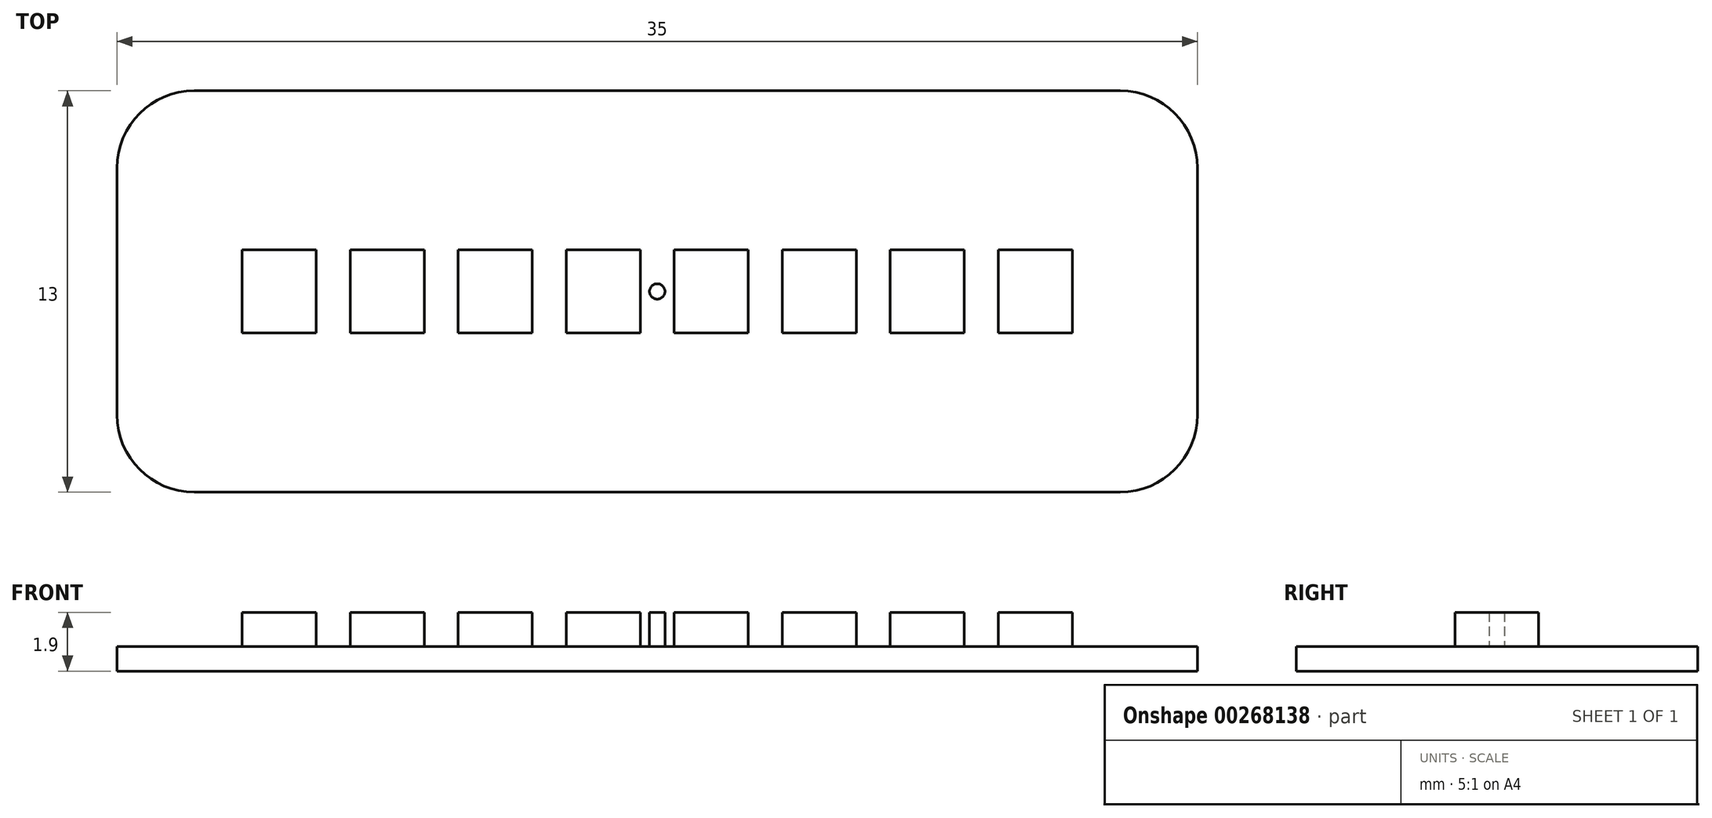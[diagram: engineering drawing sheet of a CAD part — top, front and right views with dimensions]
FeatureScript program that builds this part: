
annotation { "Feature Type Name" : "Feature", "Feature Type Description" : "" }
export const myFeature = defineFeature(function(context is Context, id is Id, definition is map)
    precondition{}
    {
        {
            var Q0;
            Q0=qCreatedBy(makeId("Top.planeOp"),FACE);
            var sketch = newSketch(context, id + "F0", { "sketchPlane" : qUnion([Q0])});
            skLineSegment(sketch, "E0.bottom", {"start": v(-17.5, 6.5) * mm, "end": v(17.5, 6.5) * mm});
            skLineSegment(sketch, "E0.top", {"start": v(-17.5, -6.5) * mm, "end": v(17.5, -6.5) * mm});
            skLineSegment(sketch, "E0.left", {"start": v(-17.5, 6.5) * mm, "end": v(-17.5, -6.5) * mm});
            skLineSegment(sketch, "E0.right", {"start": v(17.5, 6.5) * mm, "end": v(17.5, -6.5) * mm});
            skPoint(sketch, "E0.middle", {"position": v(0, 0) * mm});
            skPoint(sketch, "E1.endSnap0", {"position": v(-17.5, 0) * mm});
            skLineSegment(sketch, "E2", {"start": v(0, 0) * mm, "end": v(0, 0) * mm});
            skSolve(sketch);
        }
        {
            var Q0;
            Q0=makeQuery(id+"F0.imprint","IMPRINT",FACE,{"disambiguationData":[TD([[makeQuery(id+"F0.imprint","IMPRINT",EDGE,{"derivedFrom":sQuery(id+"F0.wireOp",EDGE,"E0.bottom")}),-1.0]])]});
            extrude(context, id + "F1", {"entities" : qUnion([Q0]), "depth" : 0.8 * mm, "offsetDistance" : 25 * mm});
        }
        {
            var Q0;
            Q0=makeQuery(id+"F1.opExtrude","CAP_FACE",FACE,{"disambiguationData":[OSD([sQuery(id+"F0.wireOp",EDGE,"E0.bottom"),sQuery(id+"F0.wireOp",EDGE,"E0.top"),sQuery(id+"F0.wireOp",EDGE,"E0.left"),sQuery(id+"F0.wireOp",EDGE,"E0.right")])],"isStart":false});
            var sketch = newSketch(context, id + "F2", { "sketchPlane" : qUnion([Q0])});
            skLineSegment(sketch, "E3", {"start": v(0.55, 1.35) * mm, "end": v(2.95, 1.35) * mm});
            skLineSegment(sketch, "E4", {"start": v(4.05, 1.35) * mm, "end": v(6.45, 1.35) * mm});
            skLineSegment(sketch, "E5", {"start": v(7.55, 1.35) * mm, "end": v(9.95, 1.35) * mm});
            skLineSegment(sketch, "E6", {"start": v(11.05, 1.35) * mm, "end": v(13.45, 1.35) * mm});
            skLineSegment(sketch, "E7", {"start": v(13.45, 1.35) * mm, "end": v(13.45, -1.35) * mm});
            skLineSegment(sketch, "E8", {"start": v(13.45, -1.35) * mm, "end": v(11.05, -1.35) * mm});
            skLineSegment(sketch, "E9", {"start": v(9.95, -1.35) * mm, "end": v(7.55, -1.35) * mm});
            skLineSegment(sketch, "E10", {"start": v(6.45, -1.35) * mm, "end": v(4.05, -1.35) * mm});
            skLineSegment(sketch, "E11", {"start": v(2.95, -1.35) * mm, "end": v(0.55, -1.35) * mm});
            skLineSegment(sketch, "E12", {"start": v(-0.55, -1.35) * mm, "end": v(-2.95, -1.35) * mm});
            skLineSegment(sketch, "E13", {"start": v(-4.05, -1.35) * mm, "end": v(-6.45, -1.35) * mm});
            skPoint(sketch, "E13.endSnap0", {"position": v(1.75, -1.35) * mm});
            skLineSegment(sketch, "E14", {"start": v(-7.55, -1.35) * mm, "end": v(-9.95, -1.35) * mm});
            skLineSegment(sketch, "E15", {"start": v(-11.05, -1.35) * mm, "end": v(-13.45, -1.35) * mm});
            skLineSegment(sketch, "E16", {"start": v(-13.45, -1.35) * mm, "end": v(-13.45, 1.35) * mm});
            skLineSegment(sketch, "E17", {"start": v(-13.45, 1.35) * mm, "end": v(-11.05, 1.35) * mm});
            skLineSegment(sketch, "E18", {"start": v(-9.95, 1.35) * mm, "end": v(-7.55, 1.35) * mm});
            skLineSegment(sketch, "E19", {"start": v(-6.45, 1.35) * mm, "end": v(-4.05, 1.35) * mm});
            skLineSegment(sketch, "E20", {"start": v(-2.95, 1.35) * mm, "end": v(-0.55, 1.35) * mm});
            skLineSegment(sketch, "E21", {"start": v(-11.05, 1.35) * mm, "end": v(-11.05, -1.35) * mm});
            skLineSegment(sketch, "E22", {"start": v(-9.95, -1.35) * mm, "end": v(-9.95, 1.35) * mm});
            skLineSegment(sketch, "E23", {"start": v(-7.55, 1.35) * mm, "end": v(-7.55, -1.35) * mm});
            skLineSegment(sketch, "E24", {"start": v(-6.45, -1.35) * mm, "end": v(-6.45, 1.35) * mm});
            skLineSegment(sketch, "E25", {"start": v(-4.05, 1.35) * mm, "end": v(-4.05, -1.35) * mm});
            skLineSegment(sketch, "E26", {"start": v(-2.95, -1.35) * mm, "end": v(-2.95, 1.35) * mm});
            skLineSegment(sketch, "E27", {"start": v(-0.55, 1.35) * mm, "end": v(-0.55, -1.35) * mm});
            skLineSegment(sketch, "E28", {"start": v(0.55, -1.35) * mm, "end": v(0.55, 1.35) * mm});
            skLineSegment(sketch, "E29", {"start": v(2.95, 1.35) * mm, "end": v(2.95, -1.35) * mm});
            skLineSegment(sketch, "E30", {"start": v(4.05, -1.35) * mm, "end": v(4.05, 1.35) * mm});
            skLineSegment(sketch, "E31", {"start": v(6.45, 1.35) * mm, "end": v(6.45, -1.35) * mm});
            skLineSegment(sketch, "E32", {"start": v(7.55, -1.35) * mm, "end": v(7.55, 1.35) * mm});
            skLineSegment(sketch, "E33", {"start": v(9.95, 1.35) * mm, "end": v(9.95, -1.35) * mm});
            skLineSegment(sketch, "E34", {"start": v(11.05, -1.35) * mm, "end": v(11.05, 1.35) * mm});
            skSolve(sketch);
        }
        {
            var Q0;
            Q0=makeQuery(id+"F2.imprint","IMPRINT",FACE,{"disambiguationData":[TD([[makeQuery(id+"F2.imprint","IMPRINT",EDGE,{"derivedFrom":sQuery(id+"F2.wireOp",EDGE,"Nh2TPCi6-N7fB-lPh8-vGMw-7dPol69uJFiX")}),1.0]])]});
            var Q1;
            Q1=makeQuery(id+"F2.imprint","IMPRINT",FACE,{"disambiguationData":[TD([[makeQuery(id+"F2.imprint","IMPRINT",EDGE,{"derivedFrom":sQuery(id+"F2.wireOp",EDGE,"IgYMUzLT-w3el-O9QX-IQLH-ZplNCAJAtdK8")}),1.0]])]});
            var Q2;
            Q2=makeQuery(id+"F2.imprint","IMPRINT",FACE,{"disambiguationData":[TD([[makeQuery(id+"F2.imprint","IMPRINT",EDGE,{"derivedFrom":sQuery(id+"F2.wireOp",EDGE,"QlsNjj8I-5FtQ-iViH-XFvM-CHFEkj7yUTcQ")}),1.0]])]});
            var Q3;
            Q3=makeQuery(id+"F2.imprint","IMPRINT",FACE,{"disambiguationData":[TD([[makeQuery(id+"F2.imprint","IMPRINT",EDGE,{"derivedFrom":sQuery(id+"F2.wireOp",EDGE,"GhbiScQi-nWAB-MW9s-JWuv-epK5emdQUspR")}),1.0]])]});
            var Q4;
            Q4=makeQuery(id+"F2.imprint","IMPRINT",FACE,{"disambiguationData":[TD([[makeQuery(id+"F2.imprint","IMPRINT",EDGE,{"derivedFrom":sQuery(id+"F2.wireOp",EDGE,"l9unKfMl-JpUO-IQut-zIk9-546266UzaAWZ")}),1.0]])]});
            var Q5;
            Q5=makeQuery(id+"F2.imprint","IMPRINT",FACE,{"disambiguationData":[TD([[makeQuery(id+"F2.imprint","IMPRINT",EDGE,{"derivedFrom":sQuery(id+"F2.wireOp",EDGE,"Xbstmt0r-Llr9-CsSF-BuOB-UmNqTWMwmW4i")}),1.0]])]});
            var Q6;
            Q6=makeQuery(id+"F2.imprint","IMPRINT",FACE,{"disambiguationData":[TD([[makeQuery(id+"F2.imprint","IMPRINT",EDGE,{"derivedFrom":sQuery(id+"F2.wireOp",EDGE,"hfTefFTx-K82Y-Gufc-tfac-qzgaFsFkcToa")}),1.0]])]});
            var Q7;
            Q7=makeQuery(id+"F2.imprint","IMPRINT",FACE,{"disambiguationData":[TD([[makeQuery(id+"F2.imprint","IMPRINT",EDGE,{"derivedFrom":sQuery(id+"F2.wireOp",EDGE,"GQtfvo6G-JABu-g0Z4-LrJG-QJxPsFvsJrtZ")}),1.0]])]});
            var Q8;
            Q8=makeQuery(id+"F2.imprint","IMPRINT",FACE,{"disambiguationData":[TD([[makeQuery(id+"F2.imprint","IMPRINT",EDGE,{"derivedFrom":sQuery(id+"F2.wireOp",EDGE,"E15")}),-1.0]])]});
            var Q9;
            Q9=makeQuery(id+"F2.imprint","IMPRINT",FACE,{"disambiguationData":[TD([[makeQuery(id+"F2.imprint","IMPRINT",EDGE,{"derivedFrom":sQuery(id+"F2.wireOp",EDGE,"E14")}),-1.0]])]});
            var Q10;
            Q10=makeQuery(id+"F2.imprint","IMPRINT",FACE,{"disambiguationData":[TD([[makeQuery(id+"F2.imprint","IMPRINT",EDGE,{"derivedFrom":sQuery(id+"F2.wireOp",EDGE,"E13")}),-1.0]])]});
            var Q11;
            Q11=makeQuery(id+"F2.imprint","IMPRINT",FACE,{"disambiguationData":[TD([[makeQuery(id+"F2.imprint","IMPRINT",EDGE,{"derivedFrom":sQuery(id+"F2.wireOp",EDGE,"E12")}),-1.0]])]});
            var Q12;
            Q12=makeQuery(id+"F2.imprint","IMPRINT",FACE,{"disambiguationData":[TD([[makeQuery(id+"F2.imprint","IMPRINT",EDGE,{"derivedFrom":sQuery(id+"F2.wireOp",EDGE,"E3")}),-1.0]])]});
            var Q13;
            Q13=makeQuery(id+"F2.imprint","IMPRINT",FACE,{"disambiguationData":[TD([[makeQuery(id+"F2.imprint","IMPRINT",EDGE,{"derivedFrom":sQuery(id+"F2.wireOp",EDGE,"E4")}),-1.0]])]});
            var Q14;
            Q14=makeQuery(id+"F2.imprint","IMPRINT",FACE,{"disambiguationData":[TD([[makeQuery(id+"F2.imprint","IMPRINT",EDGE,{"derivedFrom":sQuery(id+"F2.wireOp",EDGE,"E5")}),-1.0]])]});
            var Q15;
            Q15=makeQuery(id+"F2.imprint","IMPRINT",FACE,{"disambiguationData":[TD([[makeQuery(id+"F2.imprint","IMPRINT",EDGE,{"derivedFrom":sQuery(id+"F2.wireOp",EDGE,"E6")}),-1.0]])]});
            extrude(context, id + "F3", {"entities" : qUnion([Q0, Q1, Q2, Q3, Q4, Q5, Q6, Q7, Q8, Q9, Q10, Q11, Q12, Q13, Q14, Q15]), "operationType" : NewBodyOperationType.ADD, "depth" : 1.1 * mm, "offsetDistance" : 25 * mm});
        }
        {
            var Q0;
            Q0=makeQuery(id+"F1.opExtrude","SWEPT_EDGE",EDGE,{"disambiguationData":[OSD([sQuery(id+"F0.wireOp",EDGE,"E0.bottom"),sQuery(id+"F0.wireOp",EDGE,"E0.left")])]});
            var Q1;
            Q1=makeQuery(id+"F1.opExtrude","SWEPT_EDGE",EDGE,{"disambiguationData":[OSD([sQuery(id+"F0.wireOp",EDGE,"E0.top"),sQuery(id+"F0.wireOp",EDGE,"E0.left")])]});
            var Q2;
            Q2=makeQuery(id+"F1.opExtrude","SWEPT_EDGE",EDGE,{"disambiguationData":[OSD([sQuery(id+"F0.wireOp",EDGE,"E0.top"),sQuery(id+"F0.wireOp",EDGE,"E0.right")])]});
            var Q3;
            Q3=makeQuery(id+"F1.opExtrude","SWEPT_EDGE",EDGE,{"disambiguationData":[OSD([sQuery(id+"F0.wireOp",EDGE,"E0.bottom"),sQuery(id+"F0.wireOp",EDGE,"E0.right")])]});
            fillet(context, id + "F4", {"entities" : qUnion([Q0, Q1, Q2, Q3]), "radius" : 2.5 * mm, "tangentPropagation" : true, "allowEdgeOverflow" : false});
        }
        {
            var Q0;
            Q0=makeQuery(id+"F1.opExtrude","CAP_FACE",FACE,{"disambiguationData":[OSD([sQuery(id+"F0.wireOp",EDGE,"E0.bottom"),sQuery(id+"F0.wireOp",EDGE,"E0.top"),sQuery(id+"F0.wireOp",EDGE,"E0.left"),sQuery(id+"F0.wireOp",EDGE,"E0.right")])],"isStart":false});
            var sketch = newSketch(context, id + "F5", { "sketchPlane" : qUnion([Q0])});
            skCircle(sketch, "E35", {"center": v(0, 0) * mm, "radius": 0.25 * mm});
            skSolve(sketch);
        }
        {
            var Q0;
            Q0 = qSketchRegion(id + "F5", true);
            extrude(context, id + "F6", {"entities" : qUnion([Q0]), "operationType" : NewBodyOperationType.ADD, "depth" : 1.1 * mm, "offsetDistance" : 25 * mm});
        }
    });
